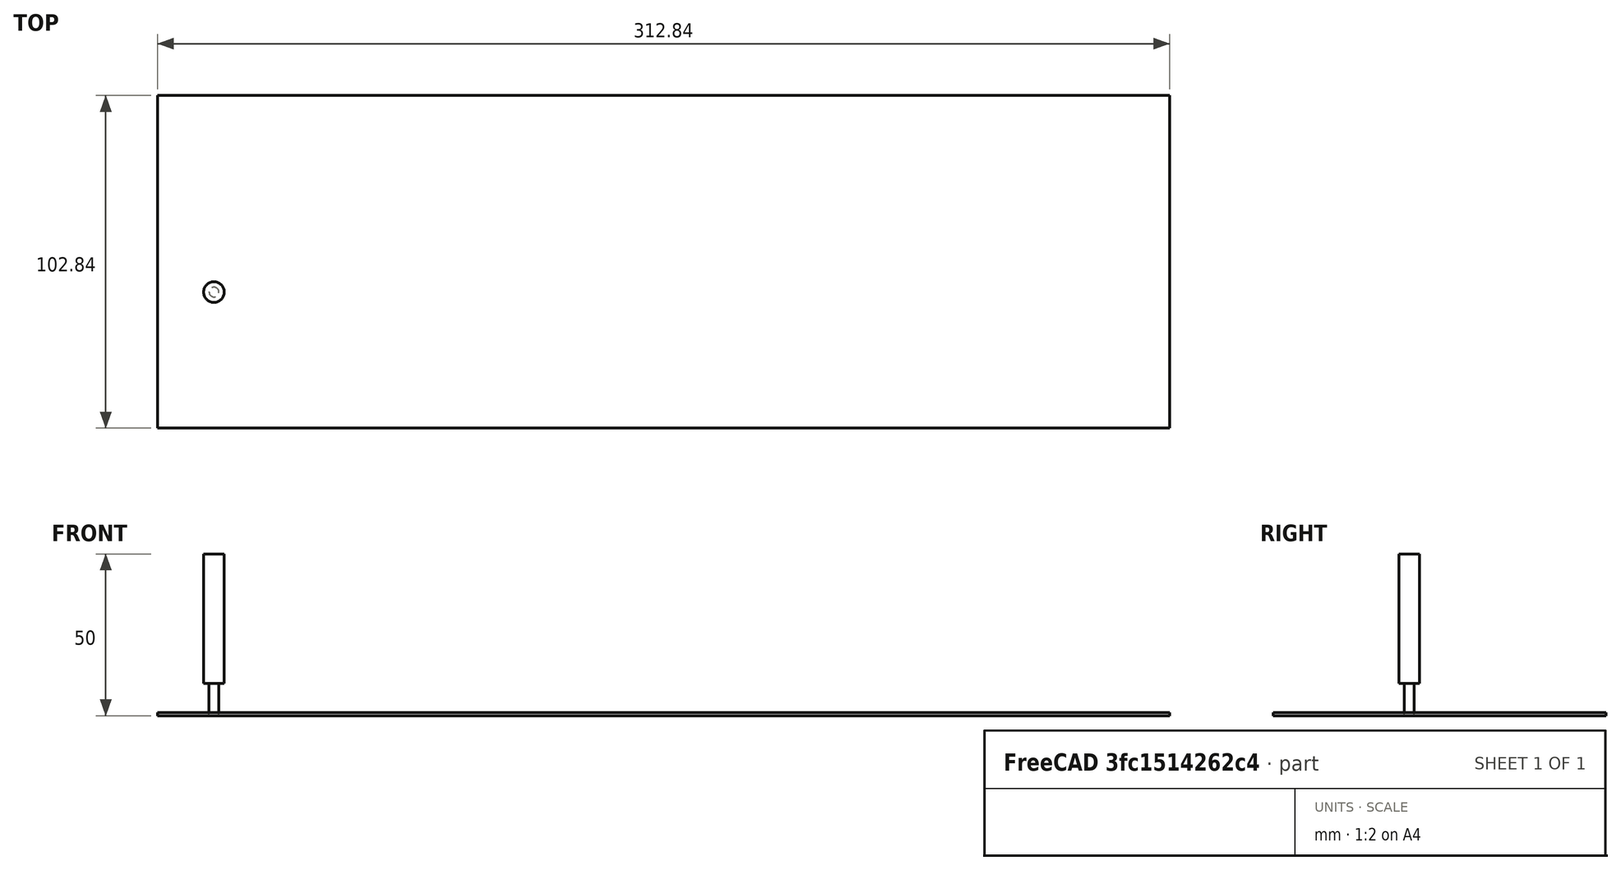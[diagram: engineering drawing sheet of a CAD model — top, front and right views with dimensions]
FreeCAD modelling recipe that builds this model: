
FCSTD DOCUMENT  (FreeCAD 0.20RUnknown)
Label: CursiveText
License: All rights reserved
LicenseURL: http://en.wikipedia.org/wiki/All_rights_reserved
objects: Path::FeaturePython×4, App::DocumentObjectGroup×3, Part::Part2DObjectPython×2, Part::FeaturePython×2, App::FeaturePython×1, PartDesign::Body×1
note: 7 computed .brp shape members not serialized (recipe doc carries the construction recipe); baked Part::Feature solids carry a one-line shape summary decoded from their .brp

FEATURE [Part::Part2DObjectPython] ShapeString  # Draft 2D object (typed FeaturePython)
  FontFile = <userpath>/MensShed/CNCRouter/dbond/Parisienne_regular.ttf
  MakeFace = true
  Placement = pos=(-16.12,-12.36,0) rot=(0,0,1;0rad)
  Size = 90
  String = thankful
  Tracking = 0
FEATURE [App::FeaturePython] SetupSheet  # Path/CAM operation (typed FeaturePython)
  ClearanceHeightExpression = OpStockZMax+SetupSheet.ClearanceHeightOffset
  ClearanceHeightOffset = 5
  CoolantMode = 0
  CoolantModes = None | Flood | Mist
  FinalDepthExpression = OpFinalDepth
  HorizRapid = 0
  SafeHeightExpression = OpStockZMax+SetupSheet.SafeHeightOffset
  SafeHeightOffset = 3
  StartDepthExpression = OpStartDepth
  StepDownExpression = OpToolDiameter
  VertRapid = 0
FEATURE [Part::Part2DObjectPython] Clone2D  label="Model-ShapeString"  # Draft 2D object (typed FeaturePython)
  Fuse = false
  Objects = -> [ShapeString]
  PathResource = Model
  Placement = pos=(-16.12,-12.36,0) rot=(0,0,1;0rad)
  Scale = (1,1,1)
FEATURE [App::DocumentObjectGroup] Model
  Group = -> [Clone2D]
FEATURE [Part::FeaturePython] Stock001  # WARN: FeaturePython — macro-defined, semantics opaque (R4)
  Height = 1
  Length = 312.84
  Placement = pos=(-17.4426,-42.0374,0) rot=(0,0,1;0rad)
  StockType = CreateBox
  Width = 102.84
FEATURE [Part::FeaturePython] ToolBit001  label="3mm_Endmill"  # Path/CAM toolbit (typed FeaturePython)
  BitPropertyNames = Chipload | CuttingEdgeHeight | Diameter | Flutes | Length | Material | ShankDiameter | SpindleDirection
  BitShape = <path>
  Chipload = 0
  CuttingEdgeHeight = 10
  Diameter = 3
  File = <userpath>/MensShed/CNCRouter/FreeCAD/Bit/3mm_Endmill.fctb
  Flutes = 0
  Length = 50
  Material = 0
  ShankDiameter = 6.4
  ShapeName = endmill
  SpindleDirection = 0
FEATURE [Path::FeaturePython] _mm_Endmill  label="3mm_Endmill001"  # Path/CAM operation (typed FeaturePython)
  HorizFeed = 10
  HorizRapid = 0
  SpindleDir = 0
  SpindleSpeed = 12000
  Tool = -> ToolBit001
  ToolNumber = 2
  VertFeed = 1.66667
  VertRapid = 0
  expr: HorizRapid = SetupSheet.HorizRapid
  expr: VertRapid = SetupSheet.VertRapid
FEATURE [App::DocumentObjectGroup] Tools
  Group = -> [_mm_Endmill]
FEATURE [Path::FeaturePython] Profile  # Path/CAM operation (typed FeaturePython)
  Active = true
  AreaParams:
    Tolerance = 1e-07
    FitArcs = True
    Simplify = False
    CleanDistance = 0.0
    Accuracy = 0.01
    Unit = 1.0
    MinArcPoints = 4
    MaxArcPoints = 100
    ClipperScale = 10000000.0
    Fill = 0
    Coplanar = 0
    Reorient = True
    Outline = False
    Explode = False
    OpenMode = 0
    Deflection = 0.01
    SubjectFill = 0
    ClipFill = 0
    Offset = 1.5
    ExtraPass = 0
    Stepover = 0.0
    LastStepover = 0.0
    JoinType = 0
    EndType = 0
    MiterLimit = 2.0
    RoundPrecision = 0.0
    PocketMode = 0
    ToolRadius = 1.0
    PocketExtraOffset = 0.0
    PocketStepover = 0.0
    PocketLastStepover = 0.0
    FromCenter = False
    Angle = 45.0
    AngleShift = 0.0
    Shift = 0.0
    Thicken = False
    SectionCount = -1
    Stepdown = 1.0
    SectionOffset = 0.0
    SectionTolerance = 1e-06
    SectionMode = 2
    Project = False
  Base = -> [Clone2D]
  ClearanceHeight = 10
  CoolantMode = 0
  CycleTime = 00:06:31
  Direction = 0
  FinalDepth = 0
  HandleMultipleFeatures = 0
  JoinType = 0
  MiterLimit = 0.1
  OffsetExtra = 0
  OpFinalDepth = 0
  OpStartDepth = 1
  OpStockZMax = 1
  OpStockZMin = 0
  OpToolDiameter = 3
  PathParams = {'orientation': 1, 'feedrate': 10.0, 'feedrate_v': 1.6666666666666667, 'verbose': True, 'resume_height': 10.0, 'retraction': 10.0, 'return_end': True, 'preamble': False}
  SafeHeight = 10
  Side = 0
  SplitArcs = false
  StartDepth = 4
  StartPoint = (0,0,0)
  StepDown = 2
  ToolController = -> _mm_Endmill
  UseComp = true
  UseStartPoint = false
  processCircles = false
  processHoles = false
  processPerimeter = true
  expr: ClearanceHeight = 10
  expr: FinalDepth = OpFinalDepth
  expr: SafeHeight = 10
  expr: StartDepth = 4
  expr: StepDown = 2
FEATURE [PartDesign::Body] Body
  Group = -> [ShapeString]
  Origin = -> Origin
FEATURE [Path::FeaturePython] Profile001  # Path/CAM operation (typed FeaturePython)
  Active = true
  AreaParams:
    Tolerance = 1e-07
    FitArcs = True
    Simplify = False
    CleanDistance = 0.0
    Accuracy = 0.01
    Unit = 1.0
    MinArcPoints = 4
    MaxArcPoints = 100
    ClipperScale = 10000000.0
    Fill = 0
    Coplanar = 0
    Reorient = True
    Outline = False
    Explode = False
    OpenMode = 0
    Deflection = 0.01
    SubjectFill = 0
    ClipFill = 0
    Offset = -1.5
    ExtraPass = 0
    Stepover = 0.0
    LastStepover = 0.0
    JoinType = 0
    EndType = 0
    MiterLimit = 2.0
    RoundPrecision = 0.0
    PocketMode = 0
    ToolRadius = 1.0
    PocketExtraOffset = 0.0
    PocketStepover = 0.0
    PocketLastStepover = 0.0
    FromCenter = False
    Angle = 45.0
    AngleShift = 0.0
    Shift = 0.0
    Thicken = False
    SectionCount = -1
    Stepdown = 1.0
    SectionOffset = 0.0
    SectionTolerance = 1e-06
    SectionMode = 2
    Project = False
  Base = -> [Clone2D]
  ClearanceHeight = 10
  CoolantMode = 0
  CycleTime = 00:02:49
  Direction = 0
  FinalDepth = 0
  HandleMultipleFeatures = 0
  JoinType = 0
  MiterLimit = 0.1
  OffsetExtra = 0
  OpFinalDepth = 0
  OpStartDepth = 1
  OpStockZMax = 1
  OpStockZMin = 0
  OpToolDiameter = 3
  PathParams = {'orientation': 1, 'feedrate': 10.0, 'feedrate_v': 1.6666666666666667, 'verbose': True, 'resume_height': 10.0, 'retraction': 10.0, 'return_end': True, 'preamble': False, 'start': Vector (198.93084255586513, 16.48097810810126, 10.0)}
  SafeHeight = 10
  Side = 1
  SplitArcs = false
  StartDepth = 4
  StartPoint = (0,0,0)
  StepDown = 2
  ToolController = -> _mm_Endmill
  UseComp = true
  UseStartPoint = false
  processCircles = false
  processHoles = false
  processPerimeter = true
  expr: ClearanceHeight = 10
  expr: FinalDepth = OpFinalDepth
  expr: SafeHeight = 10
  expr: StartDepth = 4
  expr: StepDown = 2
FEATURE [App::DocumentObjectGroup] Operations
  Group = -> [Profile,Profile001]
FEATURE [Path::FeaturePython] Job  # Path/CAM operation (typed FeaturePython)
  CycleTime = 00:09:20
  Fixtures = G54
  GeometryTolerance = 0.01
  JobType = 0
  Model = -> Model
  Operations = -> Operations
  OrderOutputBy = 0
  PostProcessor = 2
  PostProcessorOutputFile = %D/%d.ngc
  SetupSheet = -> SetupSheet
  SplitOutput = false
  Stock = -> Stock001
  Tools = -> Tools
note: 1 file-system path scrubbed to <path> (originals preserved in the JSON sidecar)
